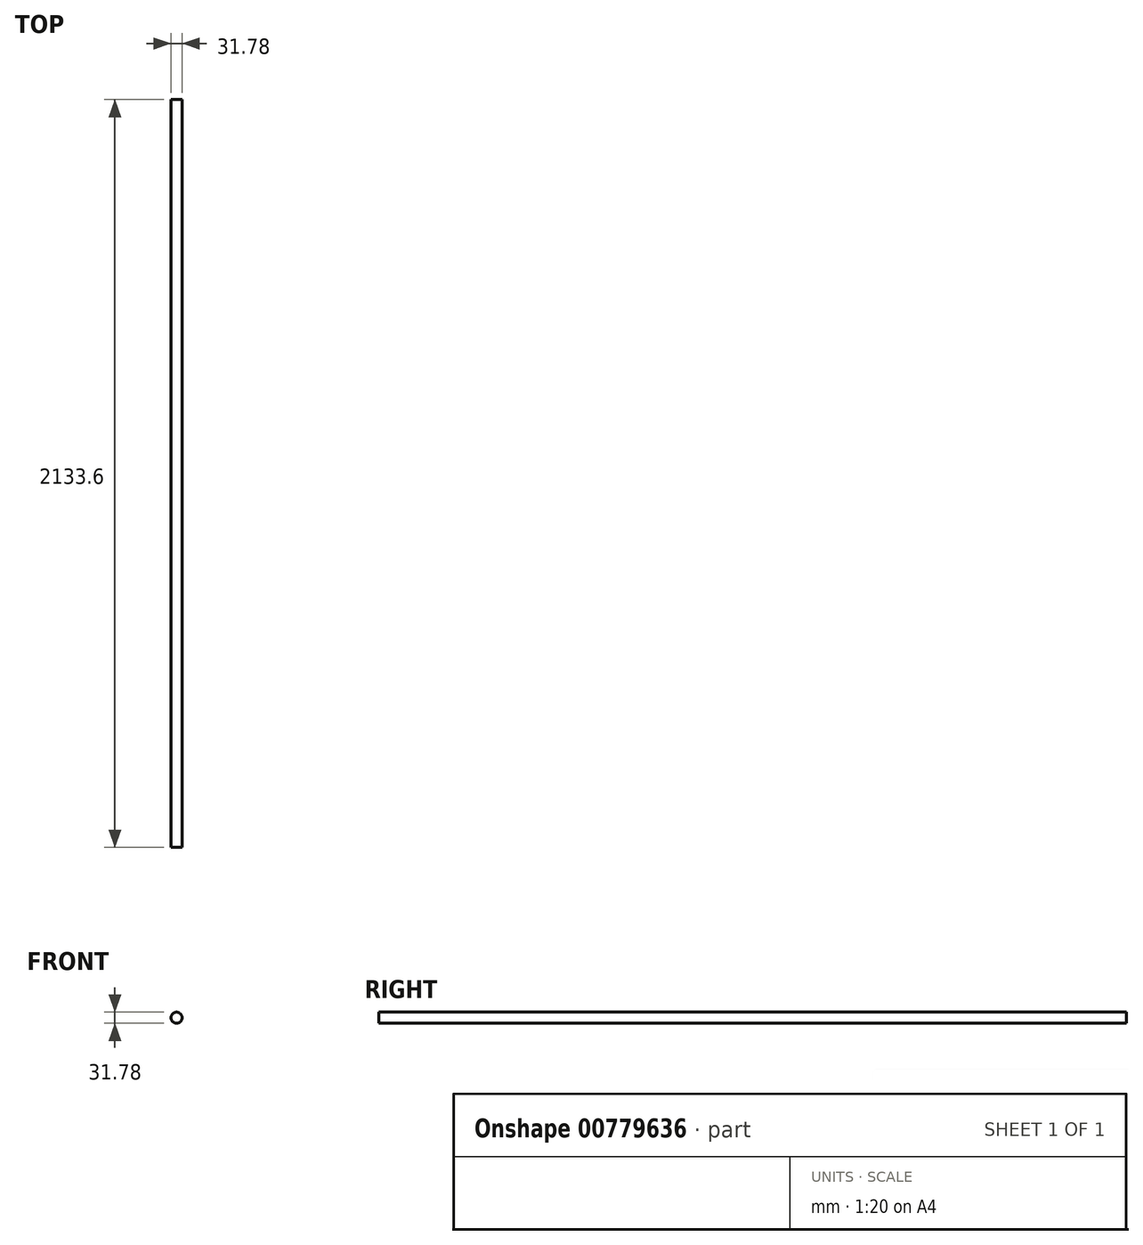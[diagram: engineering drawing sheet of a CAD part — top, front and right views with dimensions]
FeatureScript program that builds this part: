
annotation { "Feature Type Name" : "Feature", "Feature Type Description" : "" }
export const myFeature = defineFeature(function(context is Context, id is Id, definition is map)
    precondition{}
    {
        {
            var Q0;
            Q0=qCreatedBy(makeId("Front.planeOp"),FACE);
            var sketch = newSketch(context, id + "F0", { "sketchPlane" : qUnion([Q0])});
            skLineSegment(sketch, "E0.right", {"start": v(2104.4, 0) * mm, "end": v(2104.4, -31.32) * mm});
            skCircle(sketch, "E1", {"center": v(29.92, -15.88) * mm, "radius": 15.9 * mm});
            skPoint(sketch, "E1.first.point", {"position": v(30.42, 0) * mm});
            skPoint(sketch, "E1.second.point", {"position": v(29.08, -31.75) * mm});
            skPoint(sketch, "E1.third.point", {"position": v(45.8, -15.16) * mm});
            skSolve(sketch);
        }
        {
            var Q0;
            Q0=makeQuery(id+"F0.imprint","IMPRINT",FACE,{"disambiguationData":[TD([[makeQuery(id+"F0.imprint","IMPRINT",EDGE,{"derivedFrom":sQuery(id+"F0.wireOp",EDGE,"E1")}),1.0]])]});
            extrude(context, id + "F1", {"entities" : qUnion([Q0]), "endBound" : BoundingType.SYMMETRIC, "depth" : 2133.6 * mm, "offsetDistance" : 25.4 * mm});
        }
    });
